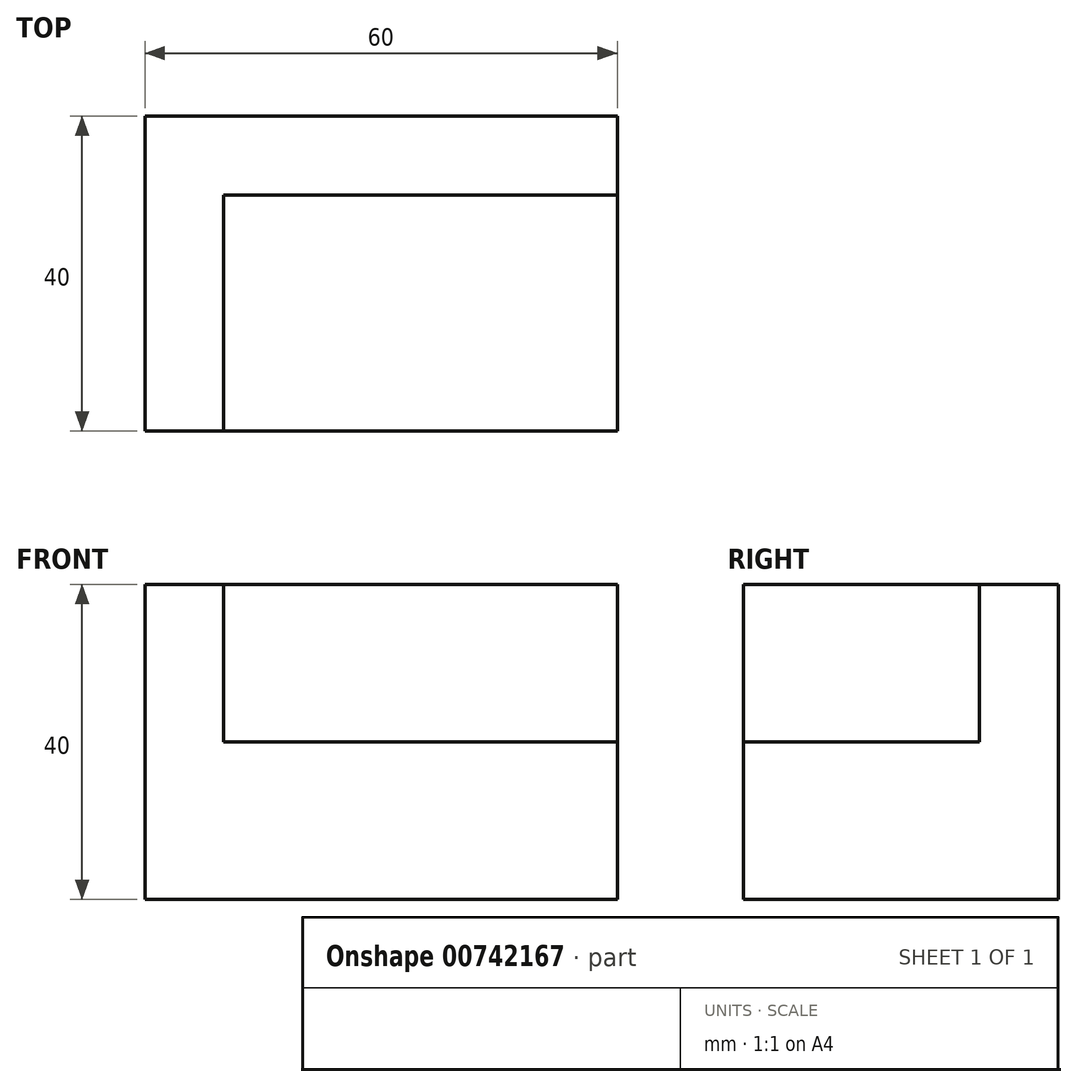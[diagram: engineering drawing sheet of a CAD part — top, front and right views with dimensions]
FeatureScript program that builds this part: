
annotation { "Feature Type Name" : "Feature", "Feature Type Description" : "" }
export const myFeature = defineFeature(function(context is Context, id is Id, definition is map)
    precondition{}
    {
        {
            var Q0;
            Q0=qCreatedBy(makeId("Front.planeOp"),FACE);
            var sketch = newSketch(context, id + "F0", { "sketchPlane" : qUnion([Q0])});
            skLineSegment(sketch, "E0", {"start": v(0, 0) * mm, "end": v(0, 40) * mm});
            skLineSegment(sketch, "E1", {"start": v(0, 40) * mm, "end": v(50, 40) * mm});
            skLineSegment(sketch, "E2", {"start": v(50, 40) * mm, "end": v(50, 0) * mm});
            skLineSegment(sketch, "E3", {"start": v(50, 0) * mm, "end": v(0, 0) * mm});
            skSolve(sketch);
        }
        {
            var Q0;
            Q0=makeQuery(id+"F0.imprint","IMPRINT",FACE,{"disambiguationData":[TD([[makeQuery(id+"F0.imprint","IMPRINT",EDGE,{"derivedFrom":sQuery(id+"F0.wireOp",EDGE,"E0")}),-1.0]])]});
            extrude(context, id + "F1", {"entities" : qUnion([Q0]), "depth" : 40 * mm, "offsetDistance" : 25 * mm});
        }
        {
            var Q0;
            Q0=makeQuery(id+"F1.opExtrude","SWEPT_FACE",FACE,{"disambiguationData":[OSD([sQuery(id+"F0.wireOp",EDGE,"E1")])]});
            var sketch = newSketch(context, id + "F2", { "sketchPlane" : qUnion([Q0])});
            skSolve(sketch);
        }
        {
            var Q0;
            {var subQ0=sQuery(id+"F0.wireOp",EDGE,"E1");Q0=makeQuery(id+"F2.imprint","IMPRINT",FACE,{"disambiguationData":[TD([[makeQuery(id+"F2.imprint","IMPRINT",EDGE,{"derivedFrom":makeQuery(id+"F1.opExtrude","CAP_EDGE",EDGE,{"disambiguationData":[OSD([subQ0])],"isStart":true})}),-1.0]])]});}
            extrude(context, id + "F3", {"entities" : qUnion([Q0]), "operationType" : NewBodyOperationType.REMOVE, "oppositeDirection" : true, "depth" : 20 * mm, "offsetDistance" : 25 * mm});
        }
        {
            var Q0;
            Q0=makeQuery(id+"F3.boolean.opBoolean","COPY",FACE,{"derivedFrom":makeQuery(id+"F3.opExtrude","CAP_FACE",FACE,{"disambiguationData":[OSD([sQuery(id+"F0.wireOp",EDGE,"E0"),sQuery(id+"F0.wireOp",EDGE,"E1"),sQuery(id+"F0.wireOp",EDGE,"E2")])],"isStart":false})});
            var sketch = newSketch(context, id + "F4", { "sketchPlane" : qUnion([Q0])});
            skLineSegment(sketch, "E4", {"start": v(0, 0) * mm, "end": v(10, 0) * mm});
            skLineSegment(sketch, "E5", {"start": v(10, 0) * mm, "end": v(10, -40) * mm});
            skLineSegment(sketch, "E6", {"start": v(10, -40) * mm, "end": v(0, -40) * mm});
            skSolve(sketch);
        }
        {
            var Q0;
            Q0=makeQuery(id+"F4.imprint","IMPRINT",FACE,{"disambiguationData":[TD([[makeQuery(id+"F4.imprint","IMPRINT",EDGE,{"derivedFrom":sQuery(id+"F4.wireOp",EDGE,"E4")}),-1.0]])]});
            extrude(context, id + "F5", {"entities" : qUnion([Q0]), "operationType" : NewBodyOperationType.ADD, "depth" : 20 * mm, "offsetDistance" : 25 * mm});
        }
        {
            var Q0;
            Q0=makeQuery(id+"F5.opExtrude","CAP_FACE",FACE,{"disambiguationData":[OSD([sQuery(id+"F0.wireOp",EDGE,"E0"),sQuery(id+"F0.wireOp",EDGE,"E1"),sQuery(id+"F4.wireOp",EDGE,"E4"),sQuery(id+"F4.wireOp",EDGE,"E5"),sQuery(id+"F4.wireOp",EDGE,"E6")])],"isStart":false});
            var sketch = newSketch(context, id + "F6", { "sketchPlane" : qUnion([Q0])});
            skLineSegment(sketch, "E7", {"start": v(10, 0) * mm, "end": v(60, 0) * mm});
            skLineSegment(sketch, "E8", {"start": v(60, 0) * mm, "end": v(60, -10) * mm});
            skLineSegment(sketch, "E9", {"start": v(60, -10) * mm, "end": v(10, -10) * mm});
            skLineSegment(sketch, "E10", {"start": v(60, -10) * mm, "end": v(60, -20) * mm});
            skPoint(sketch, "E10.endSnap0", {"position": v(10, -20) * mm});
            skSolve(sketch);
        }
        {
            var Q0;
            {var subQ0=sQuery(id+"F6.wireOp",EDGE,"E7");Q0=makeQuery(id+"F6.imprint","IMPRINT",FACE,{"disambiguationData":[TD([[makeQuery(id+"F6.imprint","IMPRINT",EDGE,{"derivedFrom":subQ0}),-1.0]])]});}
            extrude(context, id + "F7", {"entities" : qUnion([Q0]), "operationType" : NewBodyOperationType.ADD, "oppositeDirection" : true, "depth" : 10 * mm, "offsetDistance" : 25 * mm});
        }
        {
            var Q0;
            Q0=makeQuery(id+"F3.boolean.opBoolean","COPY",FACE,{"derivedFrom":makeQuery(id+"F3.opExtrude","CAP_FACE",FACE,{"disambiguationData":[OSD([sQuery(id+"F0.wireOp",EDGE,"E0"),sQuery(id+"F0.wireOp",EDGE,"E1"),sQuery(id+"F0.wireOp",EDGE,"E2")])],"isStart":false})});
            var sketch = newSketch(context, id + "F8", { "sketchPlane" : qUnion([Q0])});
            skLineSegment(sketch, "E11", {"start": v(50, 0) * mm, "end": v(60, 0) * mm});
            skLineSegment(sketch, "E12", {"start": v(60, 0) * mm, "end": v(60, -40) * mm});
            skLineSegment(sketch, "E13", {"start": v(60, -40) * mm, "end": v(50, -40) * mm});
            skSolve(sketch);
        }
        {
            var Q0;
            Q0=makeQuery(id+"F8.imprint","IMPRINT",FACE,{"disambiguationData":[TD([[makeQuery(id+"F8.imprint","IMPRINT",EDGE,{"derivedFrom":sQuery(id+"F8.wireOp",EDGE,"E11")}),-1.0]])]});
            extrude(context, id + "F9", {"entities" : qUnion([Q0]), "operationType" : NewBodyOperationType.ADD, "oppositeDirection" : true, "depth" : 20 * mm, "offsetDistance" : 25 * mm});
        }
        {
            var Q0;
            Q0=makeQuery(id+"F7.opExtrude","SWEPT_FACE",FACE,{"disambiguationData":[OSD([sQuery(id+"F6.wireOp",EDGE,"E9")])]});
            var sketch = newSketch(context, id + "F10", { "sketchPlane" : qUnion([Q0])});
            skLineSegment(sketch, "E14", {"start": v(60, 30) * mm, "end": v(60, 20) * mm});
            skLineSegment(sketch, "E15", {"start": v(60, 20) * mm, "end": v(10, 20) * mm});
            skLineSegment(sketch, "E16", {"start": v(10, 20) * mm, "end": v(10, 30) * mm});
            skLineSegment(sketch, "E17", {"start": v(60, 20) * mm, "end": v(60, 30) * mm});
            skSolve(sketch);
        }
        {
            var Q0;
            Q0=makeQuery(id+"F10.imprint","IMPRINT",FACE,{"disambiguationData":[TD([[makeQuery(id+"F10.imprint","IMPRINT",EDGE,{"derivedFrom":sQuery(id+"F10.wireOp",EDGE,"E15")}),-1.0]])]});
            extrude(context, id + "F11", {"entities" : qUnion([Q0]), "operationType" : NewBodyOperationType.ADD, "oppositeDirection" : true, "depth" : 10 * mm, "offsetDistance" : 25 * mm});
        }
    });
